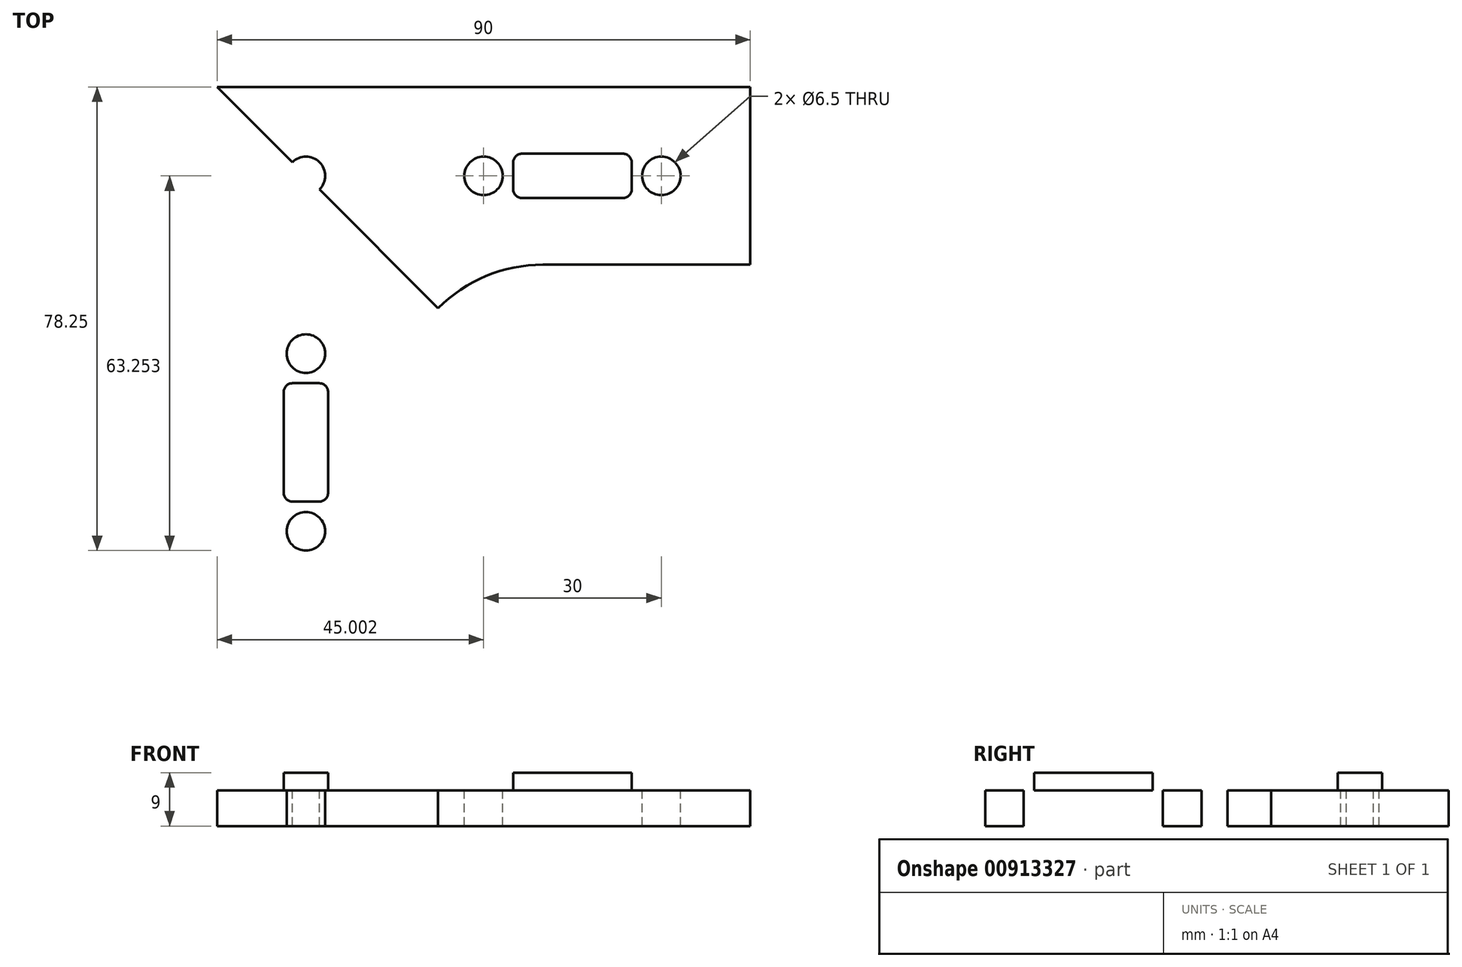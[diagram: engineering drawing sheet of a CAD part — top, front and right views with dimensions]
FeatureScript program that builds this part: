
annotation { "Feature Type Name" : "Feature", "Feature Type Description" : "" }
export const myFeature = defineFeature(function(context is Context, id is Id, definition is map)
    precondition{}
    {
        {
            var Q0;
            Q0=qCreatedBy(makeId("Top.planeOp"),FACE);
            var sketch = newSketch(context, id + "F0", { "sketchPlane" : qUnion([Q0])});
            skLineSegment(sketch, "E0.bottom", {"start": v(-58.7, 102.9) * mm, "end": v(31.3, 102.9) * mm});
            skLineSegment(sketch, "E0.top", {"start": v(-3.7, 72.9) * mm, "end": v(31.3, 72.9) * mm});
            skLineSegment(sketch, "E0.left", {"start": v(-58.7, 102.9) * mm, "end": v(-58.7, 72.9) * mm});
            skLineSegment(sketch, "E0.right", {"start": v(31.3, 102.9) * mm, "end": v(31.3, 72.9) * mm});
            skLineSegment(sketch, "E1.bottom", {"start": v(-58.7, 102.9) * mm, "end": v(-28.7, 102.9) * mm});
            skLineSegment(sketch, "E1.top", {"start": v(-58.7, 12.9) * mm, "end": v(-28.7, 12.9) * mm});
            skLineSegment(sketch, "E1.left", {"start": v(-58.7, 102.9) * mm, "end": v(-58.7, 12.9) * mm});
            skLineSegment(sketch, "E1.right", {"start": v(-28.7, 47.9) * mm, "end": v(-28.7, 12.9) * mm});
            skPoint(sketch, "E2.visualSharp", {"position": v(-28.7, 72.9) * mm});
            skArc(sketch, "E2.filletArc", {"start": v(-3.7, 72.9) * mm, "mid": v(-21.38, 65.57) * mm, "end": v(-28.7, 47.9) * mm});
            skSolve(sketch);
        }
        {
            var Q0;
            Q0=makeQuery(id+"F0.imprint","IMPRINT",FACE,{"disambiguationData":[TD([[makeQuery(id+"F0.imprint","IMPRINT",EDGE,{"derivedFrom":sQuery(id+"F0.wireOp",EDGE,"E0.bottom")}),-1.0]])]});
            extrude(context, id + "F1", {"entities" : qUnion([Q0]), "depth" : 6 * mm, "offsetDistance" : 25 * mm});
        }
        {
            var Q0;
            Q0=makeQuery(id+"F1.opExtrude","CAP_FACE",FACE,{"disambiguationData":[OSD([sQuery(id+"F0.wireOp",EDGE,"E0.bottom"),sQuery(id+"F0.wireOp",EDGE,"E0.top"),sQuery(id+"F0.wireOp",EDGE,"E0.right"),sQuery(id+"F0.wireOp",EDGE,"E1.bottom"),sQuery(id+"F0.wireOp",EDGE,"E1.top"),sQuery(id+"F0.wireOp",EDGE,"E1.left"),sQuery(id+"F0.wireOp",EDGE,"E1.right"),sQuery(id+"F0.wireOp",EDGE,"E2.filletArc")])],"isStart":false});
            var sketch = newSketch(context, id + "F2", { "sketchPlane" : qUnion([Q0])});
            skCircle(sketch, "E3", {"center": v(16.3, 87.9) * mm, "radius": 3.25 * mm});
            skPoint(sketch, "E3.centerSnap0", {"position": v(31.3, 87.9) * mm});
            skCircle(sketch, "E4", {"center": v(-13.7, 87.9) * mm, "radius": 3.25 * mm});
            skLineSegment(sketch, "E5", {"start": v(-21.38, 65.57) * mm, "end": v(-58.7, 102.9) * mm});
            skCircle(sketch, "E6.MirrorC", {"center": v(-43.7, 57.9) * mm, "radius": 3.25 * mm});
            skCircle(sketch, "E7.MirrorC", {"center": v(-43.7, 27.9) * mm, "radius": 3.25 * mm});
            skCircle(sketch, "E8", {"center": v(-43.7, 87.9) * mm, "radius": 3.25 * mm});
            skSolve(sketch);
        }
        {
            var Q0;
            Q0=makeQuery(id+"F2.imprint","IMPRINT",FACE,{"disambiguationData":[TD([[makeQuery(id+"F2.imprint","IMPRINT",EDGE,{"derivedFrom":sQuery(id+"F2.wireOp",EDGE,"E4")}),1.0]])]});
            var Q1;
            Q1=makeQuery(id+"F2.imprint","IMPRINT",FACE,{"disambiguationData":[TD([[makeQuery(id+"F2.imprint","IMPRINT",EDGE,{"derivedFrom":sQuery(id+"F2.wireOp",EDGE,"E3")}),1.0]])]});
            var Q2;
            Q2=makeQuery(id+"F2.imprint","IMPRINT",FACE,{"disambiguationData":[TD([[makeQuery(id+"F2.imprint","IMPRINT",EDGE,{"derivedFrom":sQuery(id+"F2.wireOp",EDGE,"E6.MirrorC")}),-1.0]])]});
            var Q3;
            Q3=makeQuery(id+"F2.imprint","IMPRINT",FACE,{"disambiguationData":[TD([[makeQuery(id+"F2.imprint","IMPRINT",EDGE,{"derivedFrom":sQuery(id+"F2.wireOp",EDGE,"E7.MirrorC")}),-1.0]])]});
            var Q4;
            {var subQ0=sQuery(id+"F2.wireOp",EDGE,"E8");var subQ1=sQuery(id+"F2.wireOp",EDGE,"E5");var subQ2=makeQuery(id+"F2.imprint","INTERSECT",VERTEX,{"disambiguationData":[OD(0.0)],"derivedFrom":[subQ1,subQ0]});Q4=makeQuery(id+"F2.imprint","IMPRINT",FACE,{"disambiguationData":[TD([[makeQuery(id+"F2.imprint","IMPRINT",EDGE,{"disambiguationData":[TD([[subQ2,-1.0]])],"derivedFrom":subQ1}),-1.0]])]});}
            var Q5;
            {var subQ0=sQuery(id+"F2.wireOp",EDGE,"E8");var subQ1=sQuery(id+"F2.wireOp",EDGE,"E5");var subQ2=makeQuery(id+"F2.imprint","INTERSECT",VERTEX,{"disambiguationData":[OD(0.0)],"derivedFrom":[subQ1,subQ0]});Q5=makeQuery(id+"F2.imprint","IMPRINT",FACE,{"disambiguationData":[TD([[makeQuery(id+"F2.imprint","IMPRINT",EDGE,{"disambiguationData":[TD([[subQ2,-1.0]])],"derivedFrom":subQ1}),1.0]])]});}
            extrude(context, id + "F3", {"entities" : qUnion([Q0, Q1, Q2, Q3, Q4, Q5]), "operationType" : NewBodyOperationType.REMOVE, "oppositeDirection" : true, "depth" : 8 * mm, "offsetDistance" : 25 * mm});
        }
        {
            var Q0;
            Q0=makeQuery(id+"F1.opExtrude","CAP_FACE",FACE,{"disambiguationData":[OSD([sQuery(id+"F0.wireOp",EDGE,"E0.bottom"),sQuery(id+"F0.wireOp",EDGE,"E0.top"),sQuery(id+"F0.wireOp",EDGE,"E0.right"),sQuery(id+"F0.wireOp",EDGE,"E1.bottom"),sQuery(id+"F0.wireOp",EDGE,"E1.top"),sQuery(id+"F0.wireOp",EDGE,"E1.left"),sQuery(id+"F0.wireOp",EDGE,"E1.right"),sQuery(id+"F0.wireOp",EDGE,"E2.filletArc")])],"isStart":false});
            var sketch = newSketch(context, id + "F4", { "sketchPlane" : qUnion([Q0])});
            skLineSegment(sketch, "E9.bottom", {"start": v(-7.2, 91.64) * mm, "end": v(9.8, 91.64) * mm});
            skLineSegment(sketch, "E9.top", {"start": v(-7.2, 84.14) * mm, "end": v(9.8, 84.14) * mm});
            skLineSegment(sketch, "E9.left", {"start": v(-8.7, 90.14) * mm, "end": v(-8.7, 85.64) * mm});
            skLineSegment(sketch, "E9.right", {"start": v(11.3, 90.14) * mm, "end": v(11.3, 85.64) * mm});
            skPoint(sketch, "E10.visualSharp", {"position": v(-8.7, 91.64) * mm});
            skArc(sketch, "E10.filletArc", {"start": v(-7.2, 91.64) * mm, "mid": v(-8.26, 91.2) * mm, "end": v(-8.7, 90.14) * mm});
            skPoint(sketch, "E11.visualSharp", {"position": v(11.3, 91.64) * mm});
            skArc(sketch, "E11.filletArc", {"start": v(11.3, 90.14) * mm, "mid": v(10.86, 91.2) * mm, "end": v(9.8, 91.64) * mm});
            skPoint(sketch, "E12.visualSharp", {"position": v(11.3, 84.14) * mm});
            skArc(sketch, "E12.filletArc", {"start": v(9.8, 84.14) * mm, "mid": v(10.86, 84.58) * mm, "end": v(11.3, 85.64) * mm});
            skPoint(sketch, "E13.visualSharp", {"position": v(-8.7, 84.14) * mm});
            skArc(sketch, "E13.filletArc", {"start": v(-8.7, 85.64) * mm, "mid": v(-8.26, 84.58) * mm, "end": v(-7.2, 84.14) * mm});
            skLineSegment(sketch, "E14", {"start": v(-21.38, 65.57) * mm, "end": v(-58.7, 102.9) * mm});
            skLineSegment(sketch, "E15.MirrorCS", {"start": v(-45.95, 52.9) * mm, "end": v(-41.45, 52.9) * mm});
            skArc(sketch, "E16.MirrorCS", {"start": v(-47.45, 51.4) * mm, "mid": v(-47, 52.45) * mm, "end": v(-45.95, 52.9) * mm});
            skLineSegment(sketch, "E17.MirrorCS", {"start": v(-47.45, 51.4) * mm, "end": v(-47.45, 34.4) * mm});
            skArc(sketch, "E18.MirrorCS", {"start": v(-45.95, 32.9) * mm, "mid": v(-47, 33.33) * mm, "end": v(-47.45, 34.4) * mm});
            skLineSegment(sketch, "E19.MirrorCS", {"start": v(-45.95, 32.9) * mm, "end": v(-41.45, 32.9) * mm});
            skArc(sketch, "E20.MirrorCS", {"start": v(-39.95, 34.4) * mm, "mid": v(-40.39, 33.33) * mm, "end": v(-41.45, 32.9) * mm});
            skLineSegment(sketch, "E21.MirrorCS", {"start": v(-39.95, 51.4) * mm, "end": v(-39.95, 34.4) * mm});
            skArc(sketch, "E22.MirrorCS", {"start": v(-41.45, 52.9) * mm, "mid": v(-40.39, 52.45) * mm, "end": v(-39.95, 51.4) * mm});
            skSolve(sketch);
        }
        {
            var Q0;
            Q0=makeQuery(id+"F4.imprint","IMPRINT",FACE,{"disambiguationData":[TD([[makeQuery(id+"F4.imprint","IMPRINT",EDGE,{"derivedFrom":sQuery(id+"F4.wireOp",EDGE,"E9.bottom")}),-1.0]])]});
            var Q1;
            Q1=makeQuery(id+"F4.imprint","IMPRINT",FACE,{"disambiguationData":[TD([[makeQuery(id+"F4.imprint","IMPRINT",EDGE,{"derivedFrom":sQuery(id+"F4.wireOp",EDGE,"E15.MirrorCS")}),-1.0]])]});
            extrude(context, id + "F5", {"entities" : qUnion([Q0, Q1]), "operationType" : NewBodyOperationType.ADD, "depth" : 3 * mm, "offsetDistance" : 25 * mm});
        }
    });
